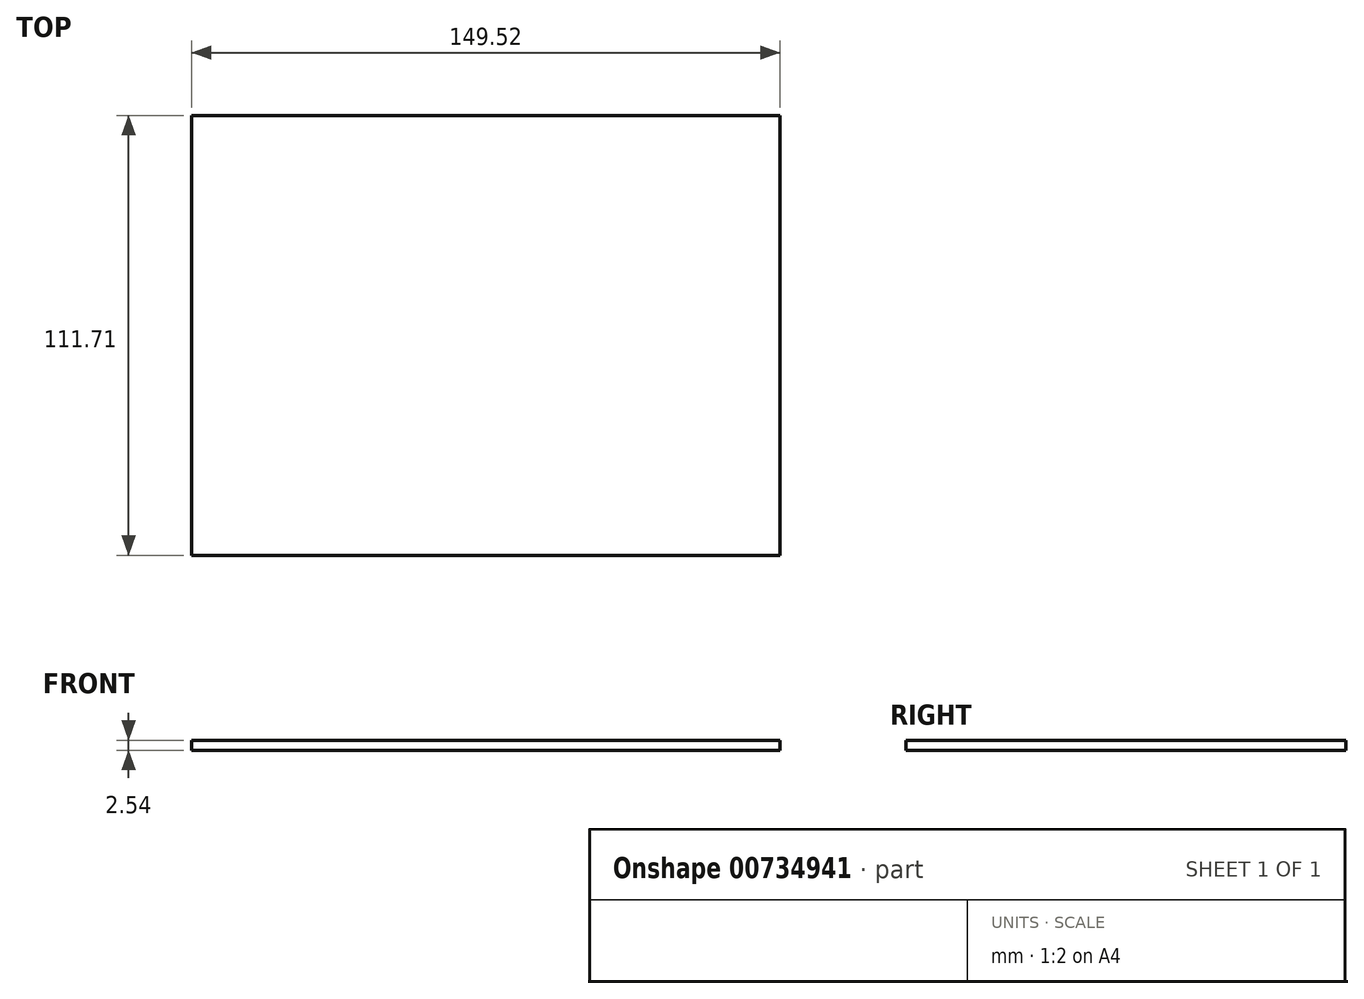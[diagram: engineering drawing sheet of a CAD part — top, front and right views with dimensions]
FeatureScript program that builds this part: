
annotation { "Feature Type Name" : "Feature", "Feature Type Description" : "" }
export const myFeature = defineFeature(function(context is Context, id is Id, definition is map)
    precondition{}
    {
        {
            var Q0;
            Q0=qCreatedBy(makeId("Top.planeOp"),FACE);
            var sketch = newSketch(context, id + "F0", { "sketchPlane" : qUnion([Q0])});
            skLineSegment(sketch, "E0", {"start": v(-75.14, 55.66) * mm, "end": v(74.38, 55.66) * mm});
            skLineSegment(sketch, "E1", {"start": v(74.38, 55.66) * mm, "end": v(74.38, -56.05) * mm});
            skLineSegment(sketch, "E2", {"start": v(74.38, -56.05) * mm, "end": v(-75.14, -56.05) * mm});
            skLineSegment(sketch, "E3", {"start": v(-75.14, -56.05) * mm, "end": v(-75.14, 55.66) * mm});
            skSolve(sketch);
        }
        {
            var Q0;
            Q0=makeQuery(id+"F0.imprint","IMPRINT",FACE,{"disambiguationData":[TD([[makeQuery(id+"F0.imprint","IMPRINT",EDGE,{"derivedFrom":sQuery(id+"F0.wireOp",EDGE,"E0")}),-1.0]])]});
            extrude(context, id + "F1", {"entities" : qUnion([Q0]), "depth" : 2.54 * mm, "offsetDistance" : 25.4 * mm});
        }
    });
